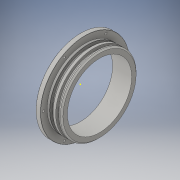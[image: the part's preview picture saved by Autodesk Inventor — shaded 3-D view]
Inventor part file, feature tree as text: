
AUTODESK INVENTOR PART (.ipt)
format: ipt  version: 2016 (Build 200138000, 138)  size: 219,136 bytes
history: native  units: in
note: dims shown in document units (in); Inventor stores cm internally (conversion verified against a paired STEP export)
features: sketch x4, extrude x2, chamfer x2, revolve x1, hole x1
ambient origin geometry x8: Origin, YZ Plane, XZ Plane, XY Plane, X Axis, Y Axis, Z Axis, Center Point
bodies: Solid1 (feature_tree)
feature tree (10):
  revolve  "Revolution1"  [1 undecoded]
  extrude  "Extrusion1"  Depth=0.13in
  extrude  "Extrusion2"  Depth=0.24in
  chamfer  "Chamfer1"  Distance=0.24in
  hole  "Hole1"  [1 undecoded]
  chamfer  "Chamfer2"  Distance=0.5in
  sketch  "Sketch8"  dims[d22=0.139in d23=0.0in d32=0.07in d33=0.125in d34=45.0deg d38=0.5in d42=0.125in d43=4.35in d44=2.3622in d46=360.0deg d48=0.1181in d49=0.75in d50=0.375in d51=0.25in d52=0.5635in d53=1.0in d54=0.8108in d55=0.01in d56=0.125in d57=45.0deg d62=3.819in d65=0.15in d66=0.15in d67=0.15in d68=0.055in d71=0.755in d72=1.68in d73=0.3in d74=0.3in]
  sketch  "Sketch2"  dims[d2=0.175in d3=0.14in]
  sketch  "Sketch3"  dims[d4=0.175in d5=0.13in]
  sketch  "Sketch5"  dims[d8=90.0deg d10=4.65in d11=0.24in d12=0.0in]
note: 2 required parameter values undecoded (feature->parameter linkage not recoverable at this tier; creation-order binding heuristic only, values carry confidence <= 0.55)